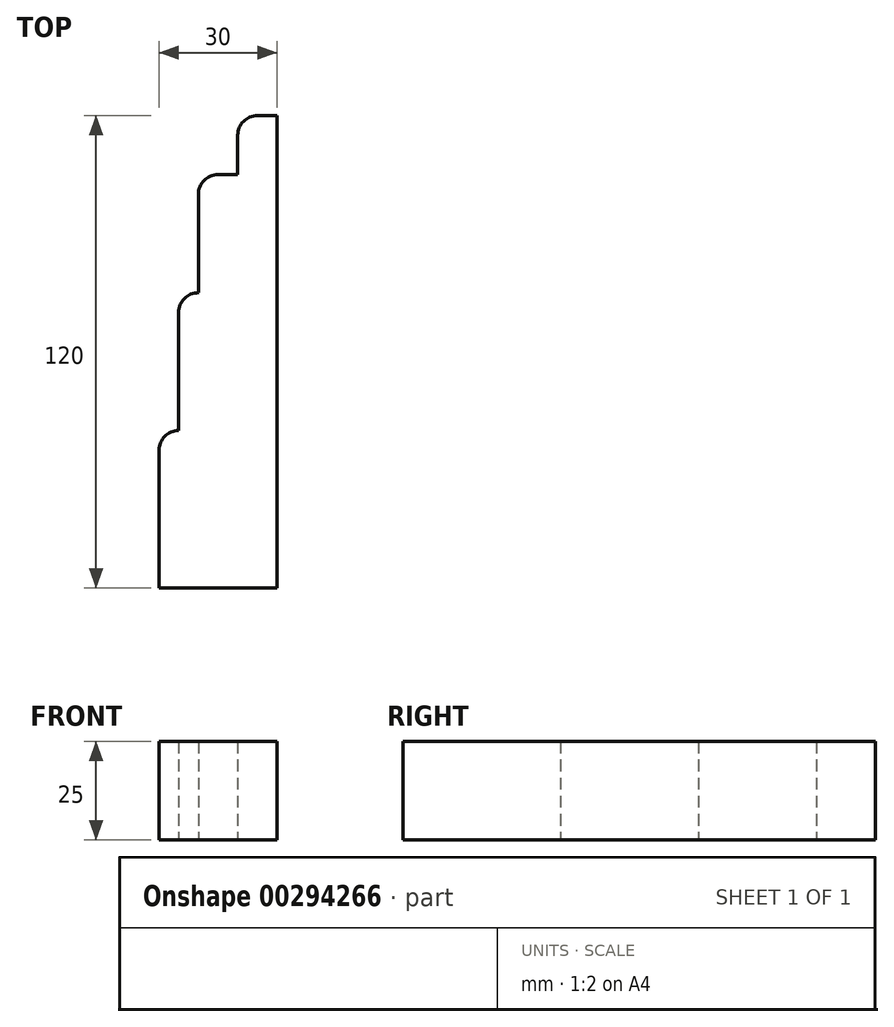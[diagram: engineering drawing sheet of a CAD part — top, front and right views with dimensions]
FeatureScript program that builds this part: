
annotation { "Feature Type Name" : "Feature", "Feature Type Description" : "" }
export const myFeature = defineFeature(function(context is Context, id is Id, definition is map)
    precondition{}
    {
        {
            var Q0;
            Q0=qCreatedBy(makeId("Top.planeOp"),FACE);
            var sketch = newSketch(context, id + "F0", { "sketchPlane" : qUnion([Q0])});
            skLineSegment(sketch, "E0", {"start": v(12.69, -39.05) * mm, "end": v(-17.31, -39.05) * mm});
            skLineSegment(sketch, "E1", {"start": v(-17.31, -39.05) * mm, "end": v(-17.31, -4.05) * mm});
            skLineSegment(sketch, "E2", {"start": v(-12.31, 0.95) * mm, "end": v(-12.31, 0.95) * mm});
            skLineSegment(sketch, "E3", {"start": v(-12.31, 0.95) * mm, "end": v(-12.31, 30.95) * mm});
            skLineSegment(sketch, "E4", {"start": v(-7.31, 35.95) * mm, "end": v(-7.31, 35.95) * mm});
            skLineSegment(sketch, "E5", {"start": v(-7.31, 35.95) * mm, "end": v(-7.31, 60.95) * mm});
            skLineSegment(sketch, "E6", {"start": v(-2.31, 65.95) * mm, "end": v(2.69, 65.95) * mm});
            skLineSegment(sketch, "E7", {"start": v(2.69, 65.95) * mm, "end": v(2.69, 75.95) * mm});
            skLineSegment(sketch, "E8", {"start": v(7.69, 80.95) * mm, "end": v(12.69, 80.95) * mm});
            skLineSegment(sketch, "E9", {"start": v(12.69, 80.95) * mm, "end": v(12.69, -39.05) * mm});
            skPoint(sketch, "E10.visualSharp", {"position": v(-17.31, 0.95) * mm});
            skArc(sketch, "E10.filletArc", {"start": v(-12.31, 0.95) * mm, "mid": v(-15.85, -0.51) * mm, "end": v(-17.31, -4.05) * mm});
            skPoint(sketch, "E11.visualSharp", {"position": v(-12.31, 35.95) * mm});
            skArc(sketch, "E11.filletArc", {"start": v(-7.31, 35.95) * mm, "mid": v(-10.85, 34.49) * mm, "end": v(-12.31, 30.95) * mm});
            skPoint(sketch, "E12.visualSharp", {"position": v(-7.31, 65.95) * mm});
            skArc(sketch, "E12.filletArc", {"start": v(-2.31, 65.95) * mm, "mid": v(-5.85, 64.49) * mm, "end": v(-7.31, 60.95) * mm});
            skPoint(sketch, "E13.visualSharp", {"position": v(2.69, 80.95) * mm});
            skArc(sketch, "E13.filletArc", {"start": v(7.69, 80.95) * mm, "mid": v(4.15, 79.49) * mm, "end": v(2.69, 75.95) * mm});
            skSolve(sketch);
        }
        {
            var Q0;
            Q0 = qSketchRegion(id + "F0", true);
            extrude(context, id + "F1", {"entities" : qUnion([Q0]), "depth" : 25 * mm});
        }
    });
